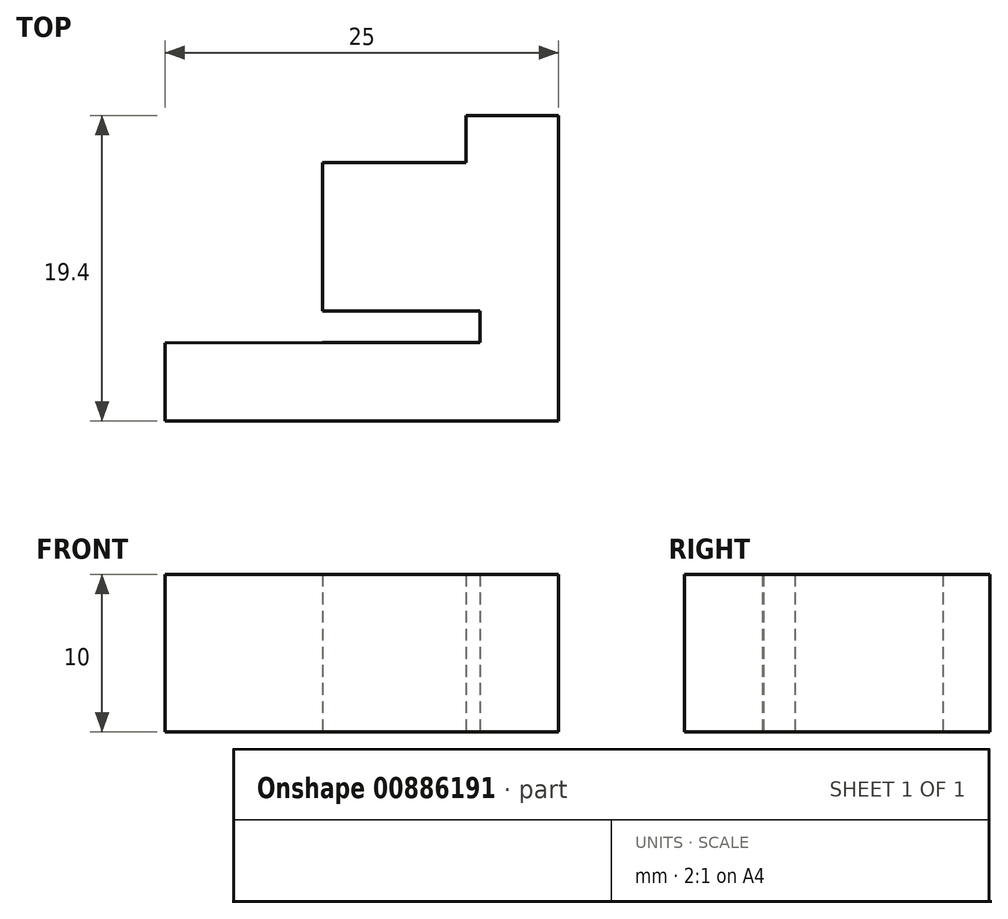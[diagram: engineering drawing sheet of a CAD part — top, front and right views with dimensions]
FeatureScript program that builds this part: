
annotation { "Feature Type Name" : "Feature", "Feature Type Description" : "" }
export const myFeature = defineFeature(function(context is Context, id is Id, definition is map)
    precondition{}
    {
        {
            var Q0;
            Q0=qCreatedBy(makeId("Top.planeOp"),FACE);
            var sketch = newSketch(context, id + "F0", { "sketchPlane" : qUnion([Q0])});
            skLineSegment(sketch, "E0", {"start": v(0, 0) * mm, "end": v(-15, 0) * mm});
            skLineSegment(sketch, "E1", {"start": v(-15, 5) * mm, "end": v(-5, 5) * mm});
            skLineSegment(sketch, "E2", {"start": v(-5, 5) * mm, "end": v(-5, 7) * mm});
            skLineSegment(sketch, "E3", {"start": v(-5, 7) * mm, "end": v(-15, 7) * mm});
            skLineSegment(sketch, "E4", {"start": v(-15, 7) * mm, "end": v(-15, 16.4) * mm});
            skLineSegment(sketch, "E5", {"start": v(0, 0) * mm, "end": v(0, 19.4) * mm});
            skLineSegment(sketch, "E6", {"start": v(0, 19.4) * mm, "end": v(-5.9, 19.4) * mm});
            skLineSegment(sketch, "E7", {"start": v(-5.9, 19.4) * mm, "end": v(-5.9, 16.4) * mm});
            skLineSegment(sketch, "E8", {"start": v(-5.9, 16.4) * mm, "end": v(-13.9, 16.4) * mm});
            skLineSegment(sketch, "E9", {"start": v(-5, 7) * mm, "end": v(0, 7) * mm});
            skLineSegment(sketch, "E10", {"start": v(-15, 0) * mm, "end": v(-25, 0) * mm});
            skLineSegment(sketch, "E11", {"start": v(-25, 0) * mm, "end": v(-25, 4.95) * mm});
            skLineSegment(sketch, "E12", {"start": v(-25, 4.95) * mm, "end": v(-15, 5) * mm});
            skPoint(sketch, "E13.end.orphan", {"position": v(-13.9, 19.4) * mm});
            skPoint(sketch, "E14.end.orphan", {"position": v(-15, 19.4) * mm});
            skLineSegment(sketch, "E15", {"start": v(-15, 16.4) * mm, "end": v(-13.9, 16.4) * mm});
            skSolve(sketch);
        }
        {
            var Q0;
            Q0=makeQuery(id+"F0.imprint","IMPRINT",FACE,{"disambiguationData":[TD([[makeQuery(id+"F0.imprint","IMPRINT",EDGE,{"derivedFrom":sQuery(id+"F0.wireOp",EDGE,"E3")}),-1.0]])]});
            var Q1;
            {var subQ1=sQuery(id+"F0.wireOp",EDGE,"E0");Q1=makeQuery(id+"F0.imprint","IMPRINT",FACE,{"disambiguationData":[TD([[makeQuery(id+"F0.imprint","IMPRINT",EDGE,{"derivedFrom":subQ1}),-1.0]])]});}
            extrude(context, id + "F1", {"entities" : qUnion([Q0, Q1]), "depth" : 10 * mm, "offsetDistance" : 25 * mm});
        }
    });
